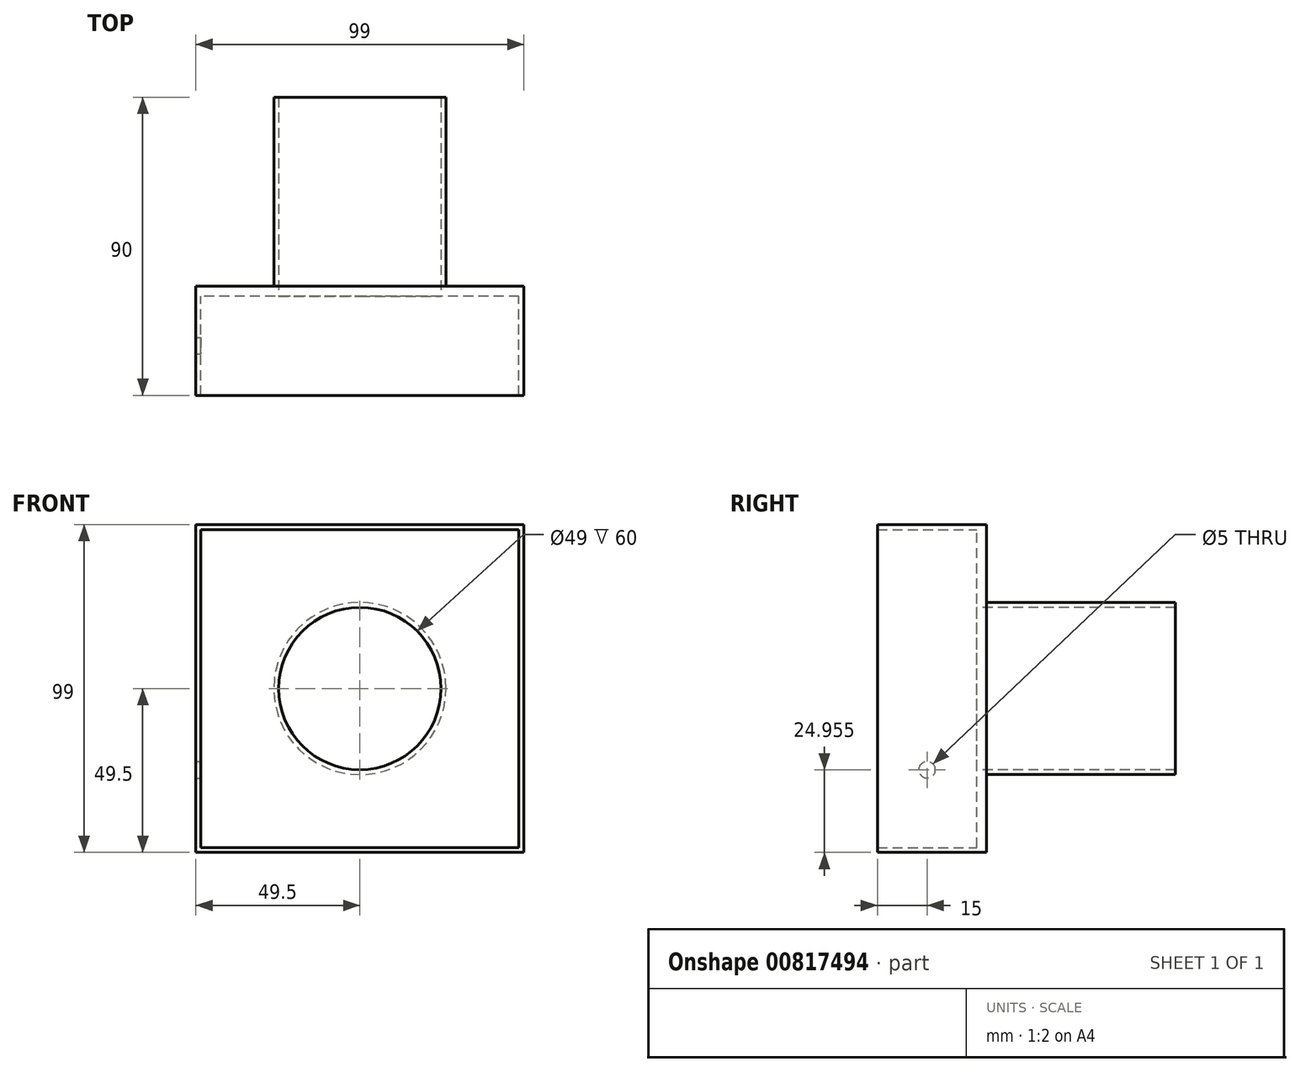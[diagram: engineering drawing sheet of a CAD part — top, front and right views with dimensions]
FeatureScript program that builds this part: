
annotation { "Feature Type Name" : "Feature", "Feature Type Description" : "" }
export const myFeature = defineFeature(function(context is Context, id is Id, definition is map)
    precondition{}
    {
        {
            var Q0;
            Q0=qCreatedBy(makeId("Front.planeOp"),FACE);
            var sketch = newSketch(context, id + "F0", { "sketchPlane" : qUnion([Q0])});
            skLineSegment(sketch, "E0.bottom", {"start": v(49.5, -49.5) * mm, "end": v(-49.5, -49.5) * mm});
            skLineSegment(sketch, "E0.top", {"start": v(49.5, 49.5) * mm, "end": v(-49.5, 49.5) * mm});
            skLineSegment(sketch, "E0.left", {"start": v(49.5, -49.5) * mm, "end": v(49.5, 49.5) * mm});
            skLineSegment(sketch, "E0.right", {"start": v(-49.5, -49.5) * mm, "end": v(-49.5, 49.5) * mm});
            skPoint(sketch, "E0.middle", {"position": v(0, 0) * mm});
            skSolve(sketch);
        }
        {
            var Q0;
            Q0=makeQuery(id+"F0.imprint","IMPRINT",FACE,{"disambiguationData":[TD([[makeQuery(id+"F0.imprint","IMPRINT",EDGE,{"derivedFrom":sQuery(id+"F0.wireOp",EDGE,"E0.bottom")}),-1.0]])]});
            extrude(context, id + "F1", {"entities" : qUnion([Q0]), "oppositeDirection" : true, "depth" : 3 * mm, "offsetDistance" : 25 * mm});
        }
        {
            var Q0;
            Q0=qCreatedBy(makeId("Front.planeOp"),FACE);
            var sketch = newSketch(context, id + "F2", { "sketchPlane" : qUnion([Q0])});
            skCircle(sketch, "E1", {"center": v(0, 0) * mm, "radius": 23 * mm});
            skCircle(sketch, "E2.0", {"center": v(0, 0) * mm, "radius": 26 * mm});
            skSolve(sketch);
        }
        {
            var Q0;
            Q0=makeQuery(id+"F2.imprint","IMPRINT",FACE,{"disambiguationData":[TD([[makeQuery(id+"F2.imprint","IMPRINT",EDGE,{"derivedFrom":sQuery(id+"F2.wireOp",EDGE,"E1")}),1.0]])]});
            var Q1;
            Q1=makeQuery(id+"F2.imprint","IMPRINT",FACE,{"disambiguationData":[TD([[makeQuery(id+"F2.imprint","IMPRINT",EDGE,{"derivedFrom":sQuery(id+"F2.wireOp",EDGE,"E1")}),-1.0]])]});
            extrude(context, id + "F3", {"entities" : qUnion([Q0, Q1]), "operationType" : NewBodyOperationType.REMOVE, "oppositeDirection" : true, "depth" : 4 * mm, "offsetDistance" : 25 * mm});
        }
        {
            var Q0;
            Q0=makeQuery(id+"F1.opExtrude","CAP_FACE",FACE,{"disambiguationData":[OSD([sQuery(id+"F0.wireOp",EDGE,"E0.bottom"),sQuery(id+"F0.wireOp",EDGE,"E0.top"),sQuery(id+"F0.wireOp",EDGE,"E0.left"),sQuery(id+"F0.wireOp",EDGE,"E0.right")])],"isStart":true});
            var sketch = newSketch(context, id + "F4", { "sketchPlane" : qUnion([Q0])});
            skCircle(sketch, "E3", {"center": v(0, 0) * mm, "radius": 24.5 * mm});
            skSolve(sketch);
        }
        {
            var Q0;
            Q0=makeQuery(id+"F4.imprint","IMPRINT",FACE,{"disambiguationData":[TD([[makeQuery(id+"F4.imprint","IMPRINT",EDGE,{"derivedFrom":sQuery(id+"F4.wireOp",EDGE,"E3")}),-1.0]])]});
            extrude(context, id + "F5", {"entities" : qUnion([Q0]), "operationType" : NewBodyOperationType.ADD, "oppositeDirection" : true, "depth" : 60 * mm, "offsetDistance" : 25 * mm});
        }
        {
            var Q0;
            Q0=qCreatedBy(makeId("Front.planeOp"),FACE);
            var sketch = newSketch(context, id + "F6", { "sketchPlane" : qUnion([Q0])});
            skLineSegment(sketch, "E4.bottom", {"start": v(49.5, -49.5) * mm, "end": v(-49.5, -49.5) * mm});
            skLineSegment(sketch, "E4.top", {"start": v(49.5, 49.5) * mm, "end": v(-49.5, 49.5) * mm});
            skLineSegment(sketch, "E4.left", {"start": v(49.5, -49.5) * mm, "end": v(49.5, 49.5) * mm});
            skLineSegment(sketch, "E4.right", {"start": v(-49.5, -49.5) * mm, "end": v(-49.5, 49.5) * mm});
            skPoint(sketch, "E4.middle", {"position": v(0, 0) * mm});
            skLineSegment(sketch, "E5.bottom", {"start": v(48, -48) * mm, "end": v(-48, -48) * mm});
            skLineSegment(sketch, "E5.top", {"start": v(48, 48) * mm, "end": v(-48, 48) * mm});
            skLineSegment(sketch, "E5.left", {"start": v(48, -48) * mm, "end": v(48, 48) * mm});
            skLineSegment(sketch, "E5.right", {"start": v(-48, -48) * mm, "end": v(-48, 48) * mm});
            skSolve(sketch);
        }
        {
            var Q0;
            Q0=makeQuery(id+"F6.imprint","IMPRINT",FACE,{"disambiguationData":[TD([[makeQuery(id+"F6.imprint","IMPRINT",EDGE,{"derivedFrom":sQuery(id+"F6.wireOp",EDGE,"E4.bottom")}),-1.0]])]});
            extrude(context, id + "F7", {"entities" : qUnion([Q0]), "operationType" : NewBodyOperationType.ADD, "depth" : 30 * mm, "offsetDistance" : 25 * mm});
        }
        {
            var Q0;
            Q0=makeQuery(id+"F7.opExtrude","SWEPT_FACE",FACE,{"disambiguationData":[OSD([sQuery(id+"F6.wireOp",EDGE,"E5.right")])]});
            var sketch = newSketch(context, id + "F8", { "sketchPlane" : qUnion([Q0])});
            skCircle(sketch, "E6", {"center": v(-15, -24.55) * mm, "radius": 2.5 * mm});
            skSolve(sketch);
        }
        {
            var Q0;
            Q0=makeQuery(id+"F8.imprint","IMPRINT",FACE,{"disambiguationData":[TD([[makeQuery(id+"F8.imprint","IMPRINT",EDGE,{"derivedFrom":sQuery(id+"F8.wireOp",EDGE,"E6")}),1.0]])]});
            extrude(context, id + "F9", {"entities" : qUnion([Q0]), "operationType" : NewBodyOperationType.REMOVE, "oppositeDirection" : true, "depth" : 25 * mm, "offsetDistance" : 25 * mm});
        }
    });
